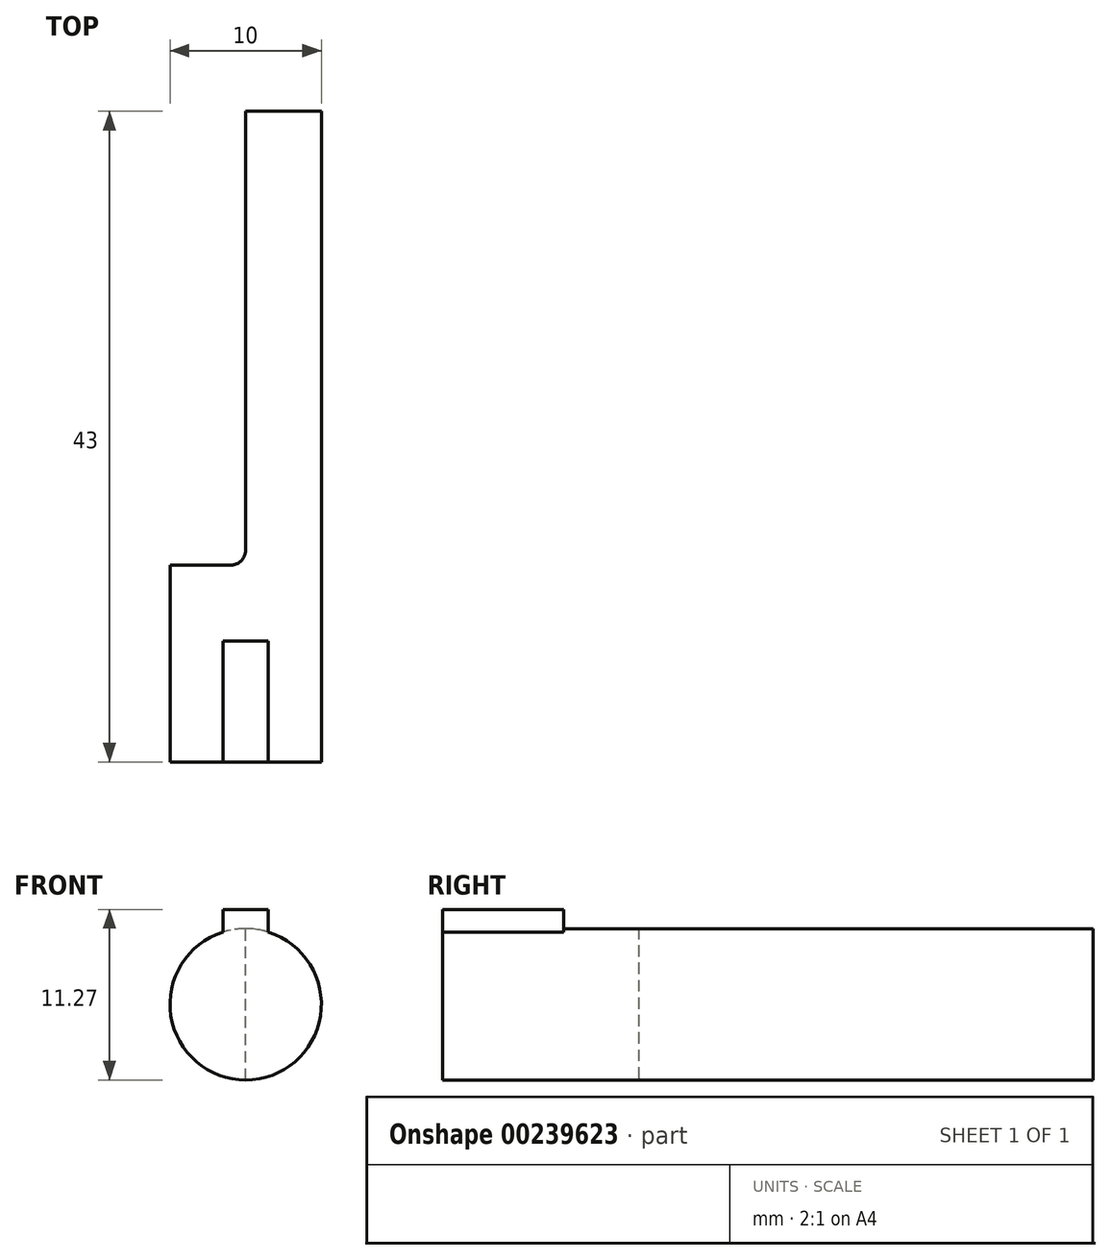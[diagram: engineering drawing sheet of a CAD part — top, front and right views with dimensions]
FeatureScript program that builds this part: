
annotation { "Feature Type Name" : "Feature", "Feature Type Description" : "" }
export const myFeature = defineFeature(function(context is Context, id is Id, definition is map)
    precondition{}
    {
        {
            var Q0;
            Q0=qCreatedBy(makeId("Front.planeOp"),FACE);
            var sketch = newSketch(context, id + "F0", { "sketchPlane" : qUnion([Q0])});
            skCircle(sketch, "E0", {"center": v(0, 0) * mm, "radius": 5 * mm});
            skSolve(sketch);
        }
        {
            var Q0;
            Q0 = qSketchRegion(id + "F0", true);
            extrude(context, id + "F1", {"entities" : qUnion([Q0]), "depth" : 43 * mm});
        }
        {
            var Q0;
            Q0=makeQuery(id+"F1.opExtrude","CAP_FACE",FACE,{"disambiguationData":[OSD([sQuery(id+"F0.wireOp",EDGE,"E0")])],"isStart":false});
            var sketch = newSketch(context, id + "F2", { "sketchPlane" : qUnion([Q0])});
            skLineSegment(sketch, "E1", {"start": v(-1.5, 4.77) * mm, "end": v(-1.5, 6.27) * mm});
            skLineSegment(sketch, "E2", {"start": v(-1.5, 6.27) * mm, "end": v(1.5, 6.27) * mm});
            skLineSegment(sketch, "E3", {"start": v(1.5, 6.27) * mm, "end": v(1.5, 4.77) * mm});
            skLineSegment(sketch, "E4", {"start": v(1.5, 4.77) * mm, "end": v(-1.5, 4.77) * mm});
            skSolve(sketch);
        }
        {
            var Q0;
            {var subQ0=sQuery(id+"F2.wireOp",EDGE,"E1");Q0=makeQuery(id+"F2.imprint","IMPRINT",FACE,{"disambiguationData":[TD([[makeQuery(id+"F2.imprint","IMPRINT",EDGE,{"derivedFrom":subQ0}),-1.0]])]});}
            extrude(context, id + "F3", {"entities" : qUnion([Q0]), "operationType" : NewBodyOperationType.ADD, "oppositeDirection" : true, "depth" : 8 * mm});
        }
        {
            var Q0;
            Q0=makeQuery(id+"F1.opExtrude","CAP_FACE",FACE,{"disambiguationData":[OSD([sQuery(id+"F0.wireOp",EDGE,"E0")])],"isStart":true});
            var sketch = newSketch(context, id + "F4", { "sketchPlane" : qUnion([Q0])});
            skLineSegment(sketch, "E5", {"start": v(0, 5) * mm, "end": v(6.12, 5) * mm});
            skLineSegment(sketch, "E6", {"start": v(6.12, 5) * mm, "end": v(6.12, -5) * mm});
            skLineSegment(sketch, "E7", {"start": v(6.12, -5) * mm, "end": v(0, -5) * mm});
            skLineSegment(sketch, "E8", {"start": v(0, -5) * mm, "end": v(0, 5) * mm});
            skSolve(sketch);
        }
        {
            var Q0;
            Q0 = qSketchRegion(id + "F4", true);
            extrude(context, id + "F5", {"entities" : qUnion([Q0]), "operationType" : NewBodyOperationType.REMOVE, "oppositeDirection" : true, "depth" : 30 * mm});
        }
        {
            var Q0;
            Q0=makeQuery(id+"F5.boolean.opBoolean","COPY",EDGE,{"derivedFrom":makeQuery(id+"F5.opExtrude","CAP_EDGE",EDGE,{"disambiguationData":[OSD([sQuery(id+"F4.wireOp",EDGE,"E8")])],"isStart":false})});
            fillet(context, id + "F6", {"entities" : qUnion([Q0]), "radius" : 1 * mm, "tangentPropagation" : true, "allowEdgeOverflow" : false});
        }
    });
